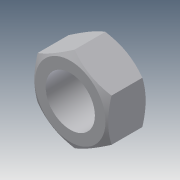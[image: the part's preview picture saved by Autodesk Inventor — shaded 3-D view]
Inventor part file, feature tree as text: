
AUTODESK INVENTOR PART (.ipt)
format: ipt  version: 2014 (Build 180170000, 170)  size: 112,128 bytes
history: native  units: in
note: dims shown in document units (in); Inventor stores cm internally (conversion verified against a paired STEP export)
features: extrude x4, sketch x4
ambient origin geometry x8: Origin, YZ Plane, XZ Plane, XY Plane, X Axis, Y Axis, Z Axis, Center Point
bodies: Solid1 (feature_tree)
feature tree (8):
  extrude  "Extrusion1"  Depth=0.3in TaperAngle=0.0deg
  extrude  "Extrusion2"  Depth=0.3in TaperAngle=0.0deg
  extrude  "Extrusion3"  Depth=0.3in TaperAngle=60.0deg
  extrude  "Extrusion4"  [1 undecoded]
  sketch  "Sketch1"  dims[d0=0.5625in d1=0.3in d2=0.0in]
  sketch  "Sketch2"  dims[d3=0.375in d4=0.3in d5=0.0in]
  sketch  "Sketch3"  dims[d6=0.3in d7=60.0deg d8=0.3in d9=60.0deg]
  sketch  "Sketch4"
note: 1 required parameter value undecoded (feature->parameter linkage not recoverable at this tier; creation-order binding heuristic only, values carry confidence <= 0.55)
